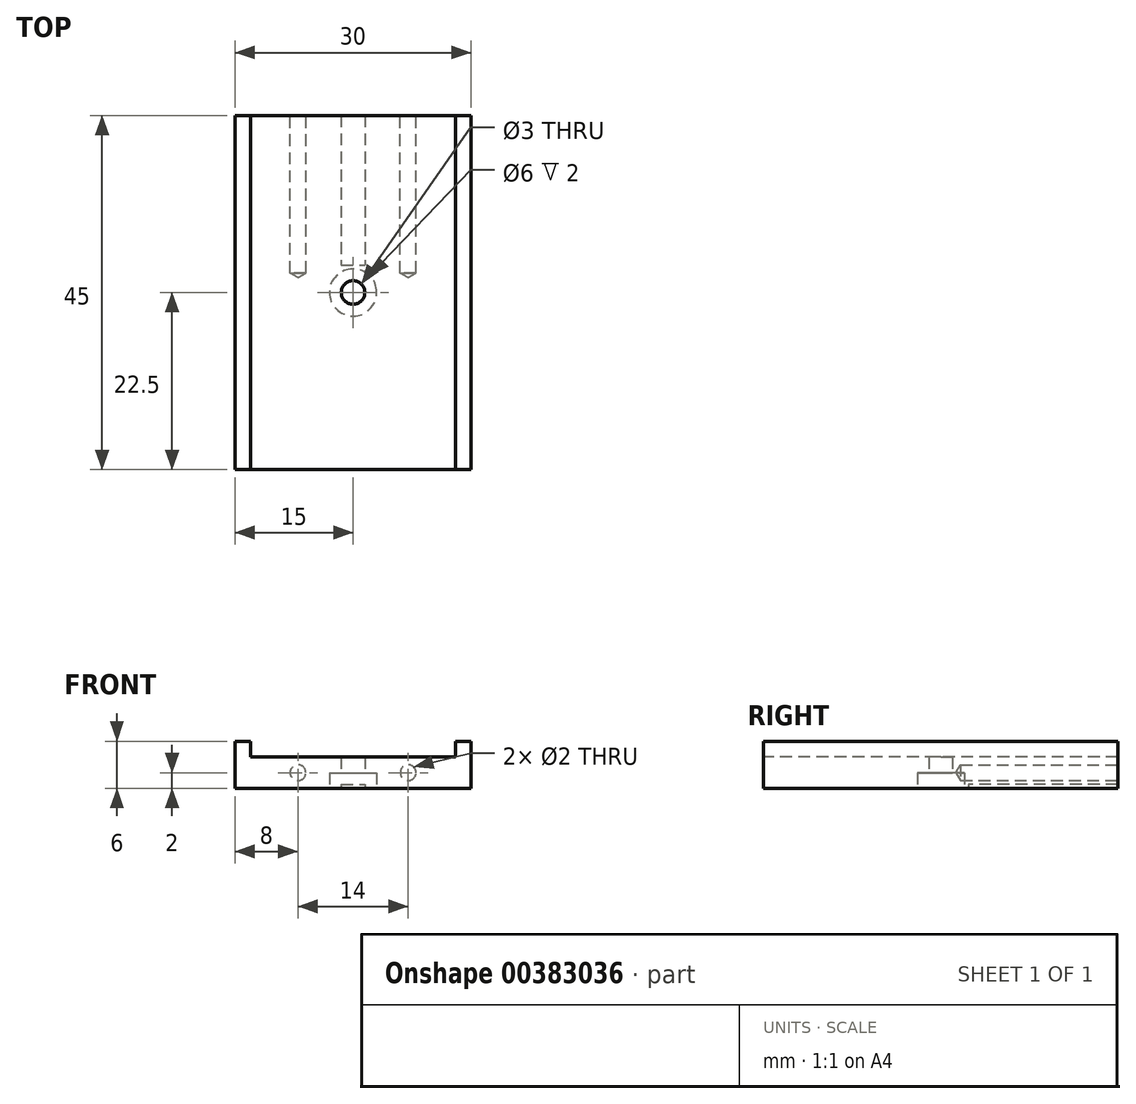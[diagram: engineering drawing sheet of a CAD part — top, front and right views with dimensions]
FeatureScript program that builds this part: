
annotation { "Feature Type Name" : "Feature", "Feature Type Description" : "" }
export const myFeature = defineFeature(function(context is Context, id is Id, definition is map)
    precondition{}
    {
        {
            var Q0;
            Q0=qCreatedBy(makeId("Top.planeOp"),FACE);
            var sketch = newSketch(context, id + "F0", { "sketchPlane" : qUnion([Q0])});
            skLineSegment(sketch, "E0.bottom", {"start": v(-15, 22.5) * mm, "end": v(15, 22.5) * mm});
            skLineSegment(sketch, "E0.top", {"start": v(-15, -22.5) * mm, "end": v(15, -22.5) * mm});
            skLineSegment(sketch, "E0.left", {"start": v(-15, 22.5) * mm, "end": v(-15, -22.5) * mm});
            skLineSegment(sketch, "E0.right", {"start": v(15, 22.5) * mm, "end": v(15, -22.5) * mm});
            skSolve(sketch);
        }
        {
            var Q0;
            Q0=makeQuery(id+"F0.imprint","IMPRINT",FACE,{"disambiguationData":[TD([[makeQuery(id+"F0.imprint","IMPRINT",EDGE,{"derivedFrom":sQuery(id+"F0.wireOp",EDGE,"E0.bottom")}),-1.0]])]});
            extrude(context, id + "F1", {"entities" : qUnion([Q0]), "depth" : 4 * mm});
        }
        {
            var Q0;
            Q0=makeQuery(id+"F1.opExtrude","SWEPT_FACE",FACE,{"disambiguationData":[OSD([sQuery(id+"F0.wireOp",EDGE,"E0.bottom")])]});
            var sketch = newSketch(context, id + "F2", { "sketchPlane" : qUnion([Q0])});
            skPoint(sketch, "E1", {"position": v(-7, 2) * mm});
            skPoint(sketch, "E2", {"position": v(7, 2) * mm});
            skSolve(sketch);
        }
        {
            var Q0;
            Q0=sQuery(id+"F2.wireOp",VERTEX,"E1");
            var Q1;
            Q1=sQuery(id+"F2.wireOp",VERTEX,"E2");
            var Q2;
            Q2=makeQuery(id+"F1.opExtrude","SWEPT_BODY",BODY,{"disambiguationData":[OSD([sQuery(id+"F0.wireOp",EDGE,"E0.bottom"),sQuery(id+"F0.wireOp",EDGE,"E0.top"),sQuery(id+"F0.wireOp",EDGE,"E0.left"),sQuery(id+"F0.wireOp",EDGE,"E0.right")])]});
            hole(context, id + "F3", {"style" : HoleStyle.SIMPLE, "endStyle" : HoleEndStyle.BLIND, "holeDiameter" : 2 * mm, "holeDepth" : 20 * mm, "isTappedThrough" : true, "tappedDepth" : 12.7 * mm, "tapClearance" : 3, "locations" : qUnion([Q0, Q1]), "scope" : qUnion([Q2])});
        }
        {
            var Q0;
            Q0=makeQuery(id+"F1.opExtrude","CAP_FACE",FACE,{"disambiguationData":[OSD([sQuery(id+"F0.wireOp",EDGE,"E0.bottom"),sQuery(id+"F0.wireOp",EDGE,"E0.top"),sQuery(id+"F0.wireOp",EDGE,"E0.left"),sQuery(id+"F0.wireOp",EDGE,"E0.right")])],"isStart":false});
            var sketch = newSketch(context, id + "F4", { "sketchPlane" : qUnion([Q0])});
            skLineSegment(sketch, "E3", {"start": v(-13, 22.5) * mm, "end": v(-13, -22.5) * mm});
            skLineSegment(sketch, "E4", {"start": v(13, 22.5) * mm, "end": v(13, -22.5) * mm});
            skSolve(sketch);
        }
        {
            var Q0;
            {var subQ0=sQuery(id+"F4.wireOp",EDGE,"E3");Q0=makeQuery(id+"F4.imprint","IMPRINT",FACE,{"disambiguationData":[TD([[makeQuery(id+"F4.imprint","IMPRINT",EDGE,{"derivedFrom":subQ0}),-1.0]])]});}
            var Q1;
            {var subQ0=sQuery(id+"F4.wireOp",EDGE,"E4");Q1=makeQuery(id+"F4.imprint","IMPRINT",FACE,{"disambiguationData":[TD([[makeQuery(id+"F4.imprint","IMPRINT",EDGE,{"derivedFrom":subQ0}),1.0]])]});}
            extrude(context, id + "F5", {"entities" : qUnion([Q0, Q1]), "operationType" : NewBodyOperationType.ADD, "depth" : 2 * mm});
        }
        {
            var Q0;
            Q0=makeQuery(id+"F1.opExtrude","CAP_FACE",FACE,{"disambiguationData":[OSD([sQuery(id+"F0.wireOp",EDGE,"E0.bottom"),sQuery(id+"F0.wireOp",EDGE,"E0.top"),sQuery(id+"F0.wireOp",EDGE,"E0.left"),sQuery(id+"F0.wireOp",EDGE,"E0.right")])],"isStart":true});
            var sketch = newSketch(context, id + "F6", { "sketchPlane" : qUnion([Q0])});
            skLineSegment(sketch, "E5.bottom", {"start": v(-1.5, -22.5) * mm, "end": v(1.5, -22.5) * mm});
            skLineSegment(sketch, "E5.top", {"start": v(-1.5, -3.5) * mm, "end": v(1.5, -3.5) * mm});
            skLineSegment(sketch, "E5.left", {"start": v(-1.5, -22.5) * mm, "end": v(-1.5, -3.5) * mm});
            skLineSegment(sketch, "E5.right", {"start": v(1.5, -22.5) * mm, "end": v(1.5, -3.5) * mm});
            skPoint(sketch, "E6", {"position": v(0, 0) * mm});
            skSolve(sketch);
        }
        {
            var Q0;
            Q0=makeQuery(id+"F6.imprint","IMPRINT",FACE,{"disambiguationData":[TD([[makeQuery(id+"F6.imprint","IMPRINT",EDGE,{"derivedFrom":sQuery(id+"F6.wireOp",EDGE,"E5.bottom")}),1.0]])]});
            extrude(context, id + "F7", {"entities" : qUnion([Q0]), "operationType" : NewBodyOperationType.REMOVE, "oppositeDirection" : true, "depth" : .5 * mm});
        }
        {
            var Q0;
            Q0=sQuery(id+"F6.wireOp",VERTEX,"E6");
            var Q1;
            Q1=makeQuery(id+"F1.opExtrude","SWEPT_BODY",BODY,{"disambiguationData":[OSD([sQuery(id+"F0.wireOp",EDGE,"E0.bottom"),sQuery(id+"F0.wireOp",EDGE,"E0.top"),sQuery(id+"F0.wireOp",EDGE,"E0.left"),sQuery(id+"F0.wireOp",EDGE,"E0.right")])]});
            hole(context, id + "F8", {"style" : HoleStyle.C_BORE, "endStyle" : HoleEndStyle.BLIND, "holeDiameter" : 3 * mm, "cBoreDiameter" : 6 * mm, "cBoreDepth" : 2 * mm, "holeDepth" : 6 * mm, "isTappedThrough" : true, "tappedDepth" : 12.7 * mm, "tapClearance" : 3, "locations" : qUnion([Q0]), "scope" : qUnion([Q1])});
        }
    });
